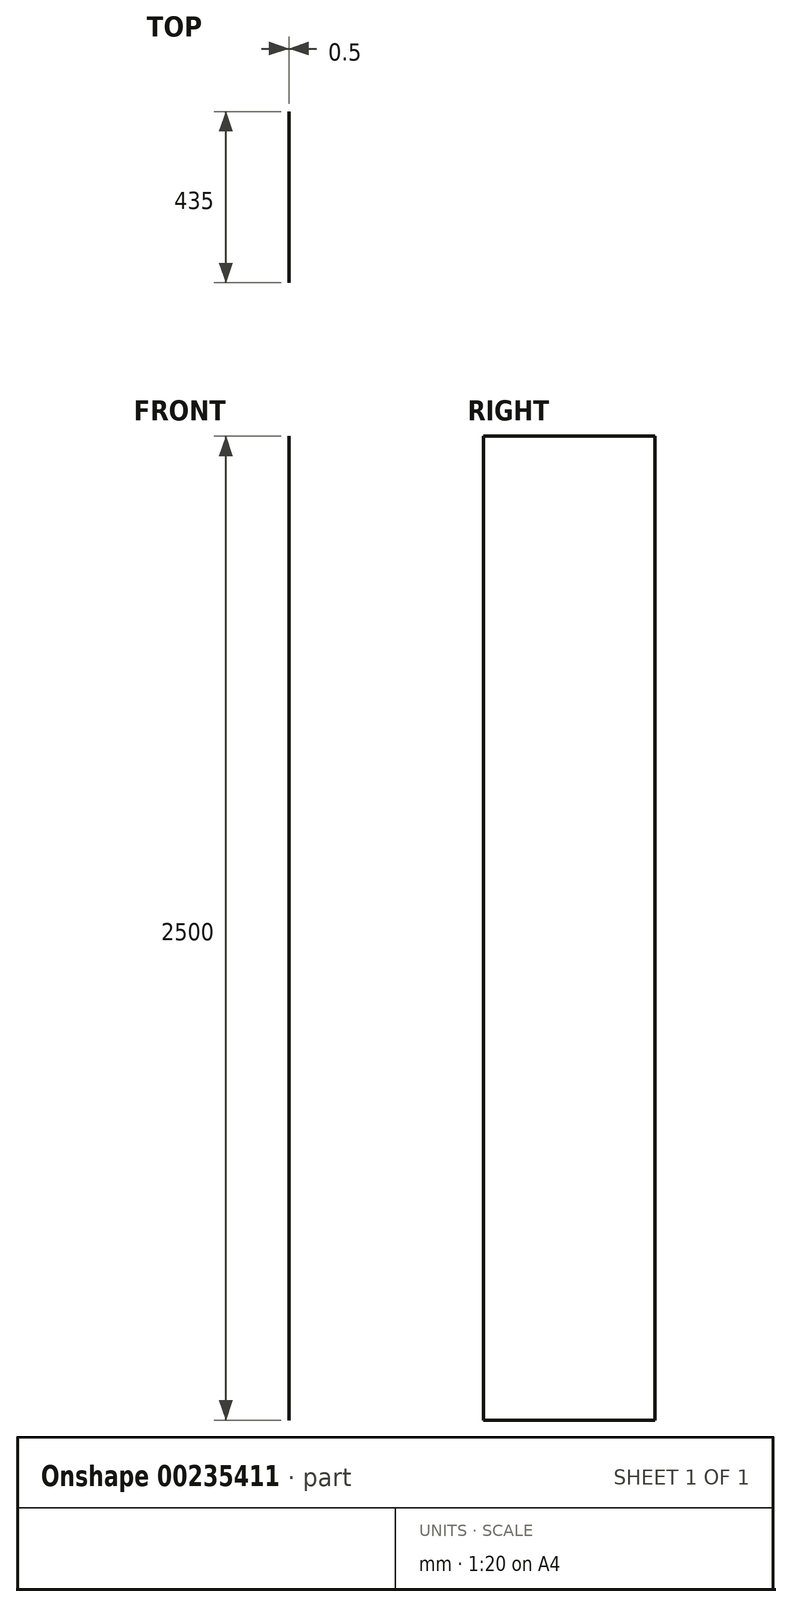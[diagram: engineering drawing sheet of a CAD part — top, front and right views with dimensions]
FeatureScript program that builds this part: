
annotation { "Feature Type Name" : "Feature", "Feature Type Description" : "" }
export const myFeature = defineFeature(function(context is Context, id is Id, definition is map)
    precondition{}
    {
        {
            var Q0;
            Q0=qCreatedBy(makeId("Right.planeOp"),FACE);
            var sketch = newSketch(context, id + "F0", { "sketchPlane" : qUnion([Q0])});
            skLineSegment(sketch, "E0.bottom", {"start": v(0, 0) * mm, "end": v(435, 0) * mm});
            skLineSegment(sketch, "E0.top", {"start": v(0, 2500) * mm, "end": v(435, 2500) * mm});
            skLineSegment(sketch, "E0.left", {"start": v(0, 0) * mm, "end": v(0, 2500) * mm});
            skLineSegment(sketch, "E0.right", {"start": v(435, 0) * mm, "end": v(435, 2500) * mm});
            skSolve(sketch);
        }
        {
            var Q0;
            Q0=makeQuery(id+"F0.imprint","IMPRINT",FACE,{"disambiguationData":[TD([[makeQuery(id+"F0.imprint","IMPRINT",EDGE,{"derivedFrom":sQuery(id+"F0.wireOp",EDGE,"E0.bottom")}),1.0]])]});
            extrude(context, id + "F1", {"entities" : qUnion([Q0]), "depth" : 0.5 * mm});
        }
    });
